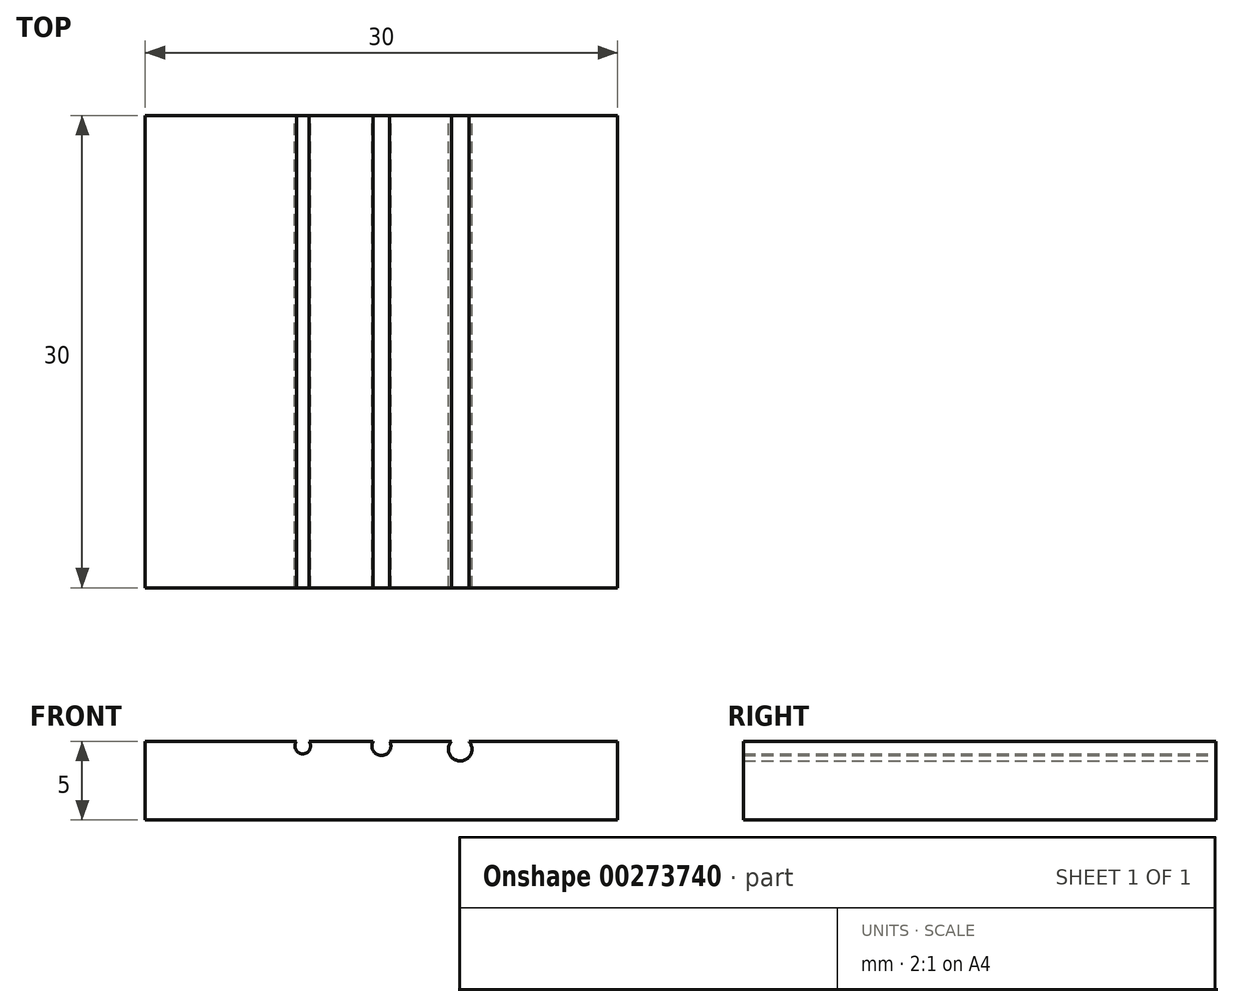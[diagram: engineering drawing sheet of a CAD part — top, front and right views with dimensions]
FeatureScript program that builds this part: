
annotation { "Feature Type Name" : "Feature", "Feature Type Description" : "" }
export const myFeature = defineFeature(function(context is Context, id is Id, definition is map)
    precondition{}
    {
        {
            var Q0;
            Q0=qCreatedBy(makeId("Front.planeOp"),FACE);
            var sketch = newSketch(context, id + "F0", { "sketchPlane" : qUnion([Q0])});
            skLineSegment(sketch, "E0.bottom", {"start": v(-30, 5) * mm, "end": v(0, 5) * mm});
            skLineSegment(sketch, "E0.top", {"start": v(-30, 0) * mm, "end": v(0, 0) * mm});
            skLineSegment(sketch, "E0.left", {"start": v(-30, 5) * mm, "end": v(-30, 0) * mm});
            skLineSegment(sketch, "E0.right", {"start": v(0, 5) * mm, "end": v(0, 0) * mm});
            skCircle(sketch, "E1", {"center": v(-20, 4.7) * mm, "radius": 0.5 * mm});
            skCircle(sketch, "E2", {"center": v(-15, 4.7) * mm, "radius": 0.6 * mm});
            skCircle(sketch, "E3", {"center": v(-10, 4.5) * mm, "radius": 0.75 * mm});
            skSolve(sketch);
        }
        {
            var Q0;
            Q0=makeQuery(id+"F0.imprint","IMPRINT",FACE,{"disambiguationData":[TD([[makeQuery(id+"F0.imprint","IMPRINT",EDGE,{"derivedFrom":sQuery(id+"F0.wireOp",EDGE,"E0.top")}),1.0]])]});
            extrude(context, id + "F1", {"entities" : qUnion([Q0]), "depth" : 30 * mm, "offsetDistance" : 25 * mm});
        }
    });
